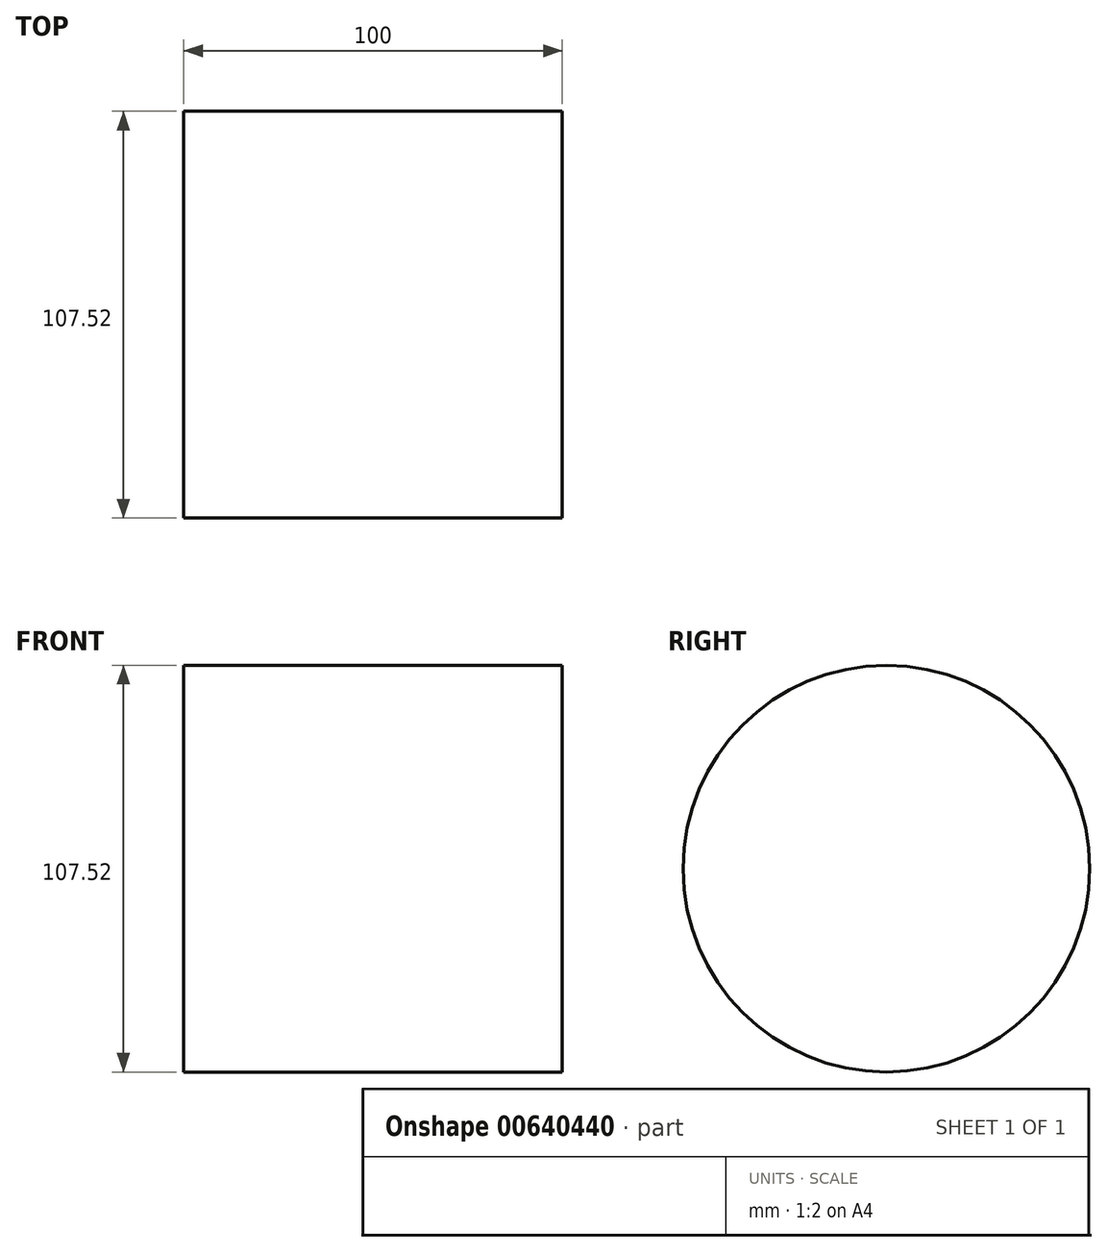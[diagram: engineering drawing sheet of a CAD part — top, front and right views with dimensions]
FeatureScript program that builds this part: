
annotation { "Feature Type Name" : "Feature", "Feature Type Description" : "" }
export const myFeature = defineFeature(function(context is Context, id is Id, definition is map)
    precondition{}
    {
        {
            var Q0;
            Q0=qCreatedBy(makeId("Right.planeOp"),FACE);
            var sketch = newSketch(context, id + "F0", { "sketchPlane" : qUnion([Q0])});
            skCircle(sketch, "E0", {"center": v(0, 1.86) * mm, "radius": 53.76 * mm});
            skSolve(sketch);
        }
        {
            var Q0;
            Q0=makeQuery(id+"F0.imprint","IMPRINT",FACE,{"disambiguationData":[TD([[makeQuery(id+"F0.imprint","IMPRINT",EDGE,{"derivedFrom":sQuery(id+"F0.wireOp",EDGE,"E0")}),1.0]])]});
            extrude(context, id + "F1", {"entities" : qUnion([Q0]), "depth" : 100 * mm, "offsetDistance" : 25.4 * mm});
        }
    });
